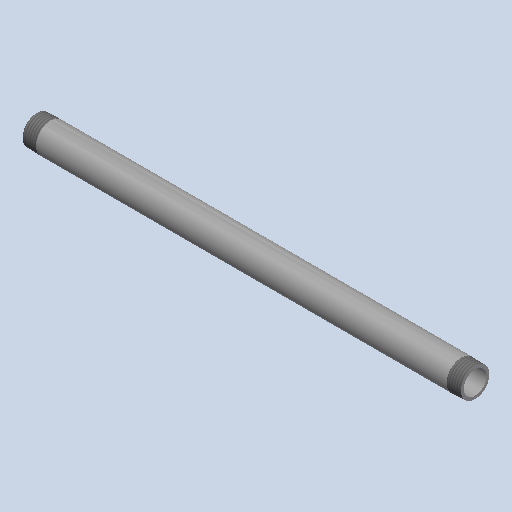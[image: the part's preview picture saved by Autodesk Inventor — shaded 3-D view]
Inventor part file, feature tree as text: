
AUTODESK INVENTOR PART (.ipt)
format: ipt  version: 2025 (Build 290162000, 162)  size: 161,280 bytes
history: native  units: mm (DEFAULTED — no unit token found)
features: other x8, revolve x1
ambient origin geometry x8: Origin, YZ Plane, XZ Plane, XY Plane, X Axis, Y Axis, Z Axis, Center Point
bodies: Solid1 (feature_tree)
feature tree (9):
  revolve  "Revolution1"  [1 undecoded]
  other  "Work Axis1"
  other  "Work Point5"
  other  "Work Axis2"
  other  "Work Point6"
  other  "Work Axis3"
  other  "Work Axis4"
  other  "Work Point7"
  other  "Work Point8"
note: 1 required parameter value undecoded (feature->parameter linkage not recoverable at this tier; creation-order binding heuristic only, values carry confidence <= 0.55)
